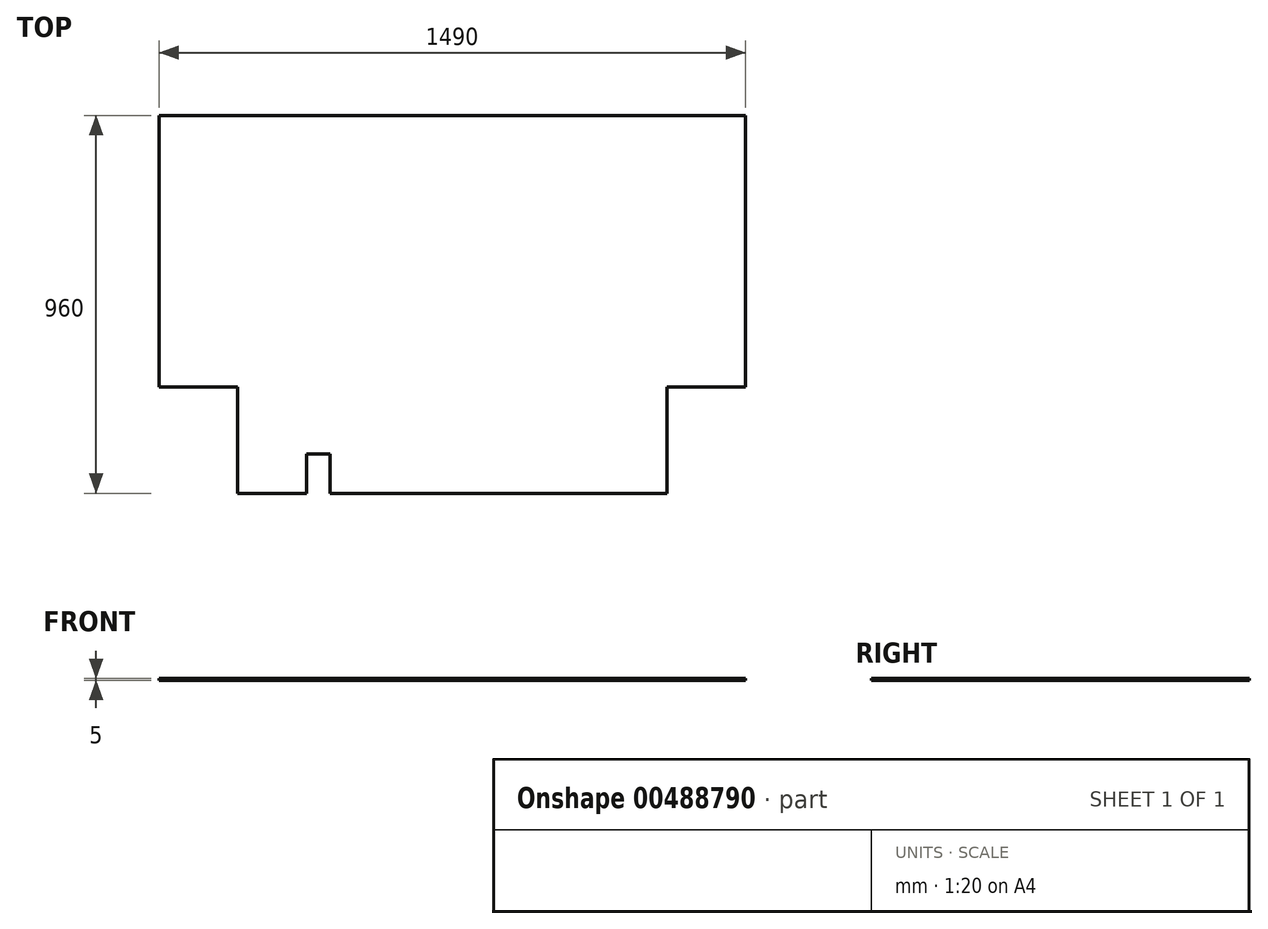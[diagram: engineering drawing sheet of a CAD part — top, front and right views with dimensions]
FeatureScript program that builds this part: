
annotation { "Feature Type Name" : "Feature", "Feature Type Description" : "" }
export const myFeature = defineFeature(function(context is Context, id is Id, definition is map)
    precondition{}
    {
        {
            var Q0;
            Q0=qCreatedBy(makeId("Top.planeOp"),FACE);
            var sketch = newSketch(context, id + "F0", { "sketchPlane" : qUnion([Q0])});
            skLineSegment(sketch, "E0.bottom", {"start": v(-787.52, 960) * mm, "end": v(702.48, 960) * mm});
            skLineSegment(sketch, "E0.top", {"start": v(-587.52, 0) * mm, "end": v(502.48, 0) * mm});
            skLineSegment(sketch, "E0.left", {"start": v(-787.52, 960) * mm, "end": v(-787.52, 270) * mm});
            skLineSegment(sketch, "E0.right", {"start": v(702.48, 960) * mm, "end": v(702.48, 270) * mm});
            skLineSegment(sketch, "E1.top", {"start": v(-787.52, 270) * mm, "end": v(-587.52, 270) * mm});
            skLineSegment(sketch, "E1.right", {"start": v(-587.52, 0) * mm, "end": v(-587.52, 270) * mm});
            skLineSegment(sketch, "E2.top", {"start": v(702.48, 270) * mm, "end": v(502.48, 270) * mm});
            skLineSegment(sketch, "E2.right", {"start": v(502.48, 0) * mm, "end": v(502.48, 270) * mm});
            skPoint(sketch, "E2.left.start.orphan", {"position": v(702.48, 0) * mm});
            skLineSegment(sketch, "E3", {"start": v(-412.52, 0) * mm, "end": v(-412.52, 100) * mm});
            skLineSegment(sketch, "E4", {"start": v(-412.52, 100) * mm, "end": v(-352.52, 100) * mm});
            skLineSegment(sketch, "E5", {"start": v(-352.52, 100) * mm, "end": v(-352.52, 0) * mm});
            skSolve(sketch);
        }
        {
            var Q0;
            Q0=makeQuery(id+"F0.imprint","IMPRINT",FACE,{"disambiguationData":[TD([[makeQuery(id+"F0.imprint","IMPRINT",EDGE,{"derivedFrom":sQuery(id+"F0.wireOp",EDGE,"E0.bottom")}),-1.0]])]});
            extrude(context, id + "F1", {"entities" : qUnion([Q0]), "flatOperationType" : FlatOperationType.REMOVE, "offsetDistance" : 25 * mm, "depth" : 5 * mm, "domain" : OperationDomain.MODEL});
        }
        {
            var Q0;
            Q0 = qSketchRegion(id + "F0", true);
            extrude(context, id + "F2", {"entities" : qUnion([Q0]), "operationType" : NewBodyOperationType.REMOVE, "oppositeDirection" : true, "depth" : 25 * mm, "offsetDistance" : 25 * mm});
        }
    });
